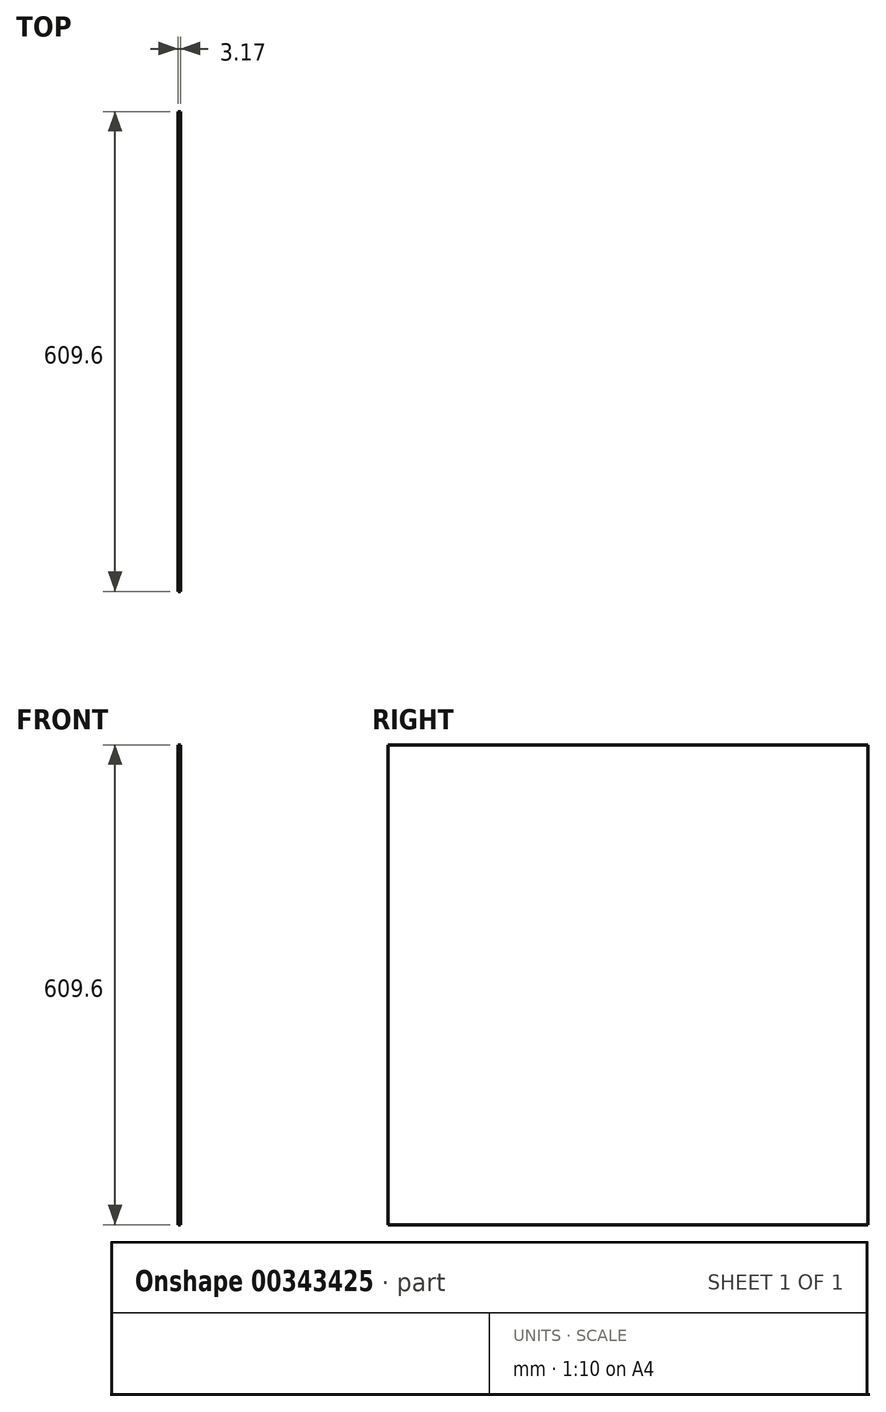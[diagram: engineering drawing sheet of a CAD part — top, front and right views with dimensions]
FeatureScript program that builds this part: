
annotation { "Feature Type Name" : "Feature", "Feature Type Description" : "" }
export const myFeature = defineFeature(function(context is Context, id is Id, definition is map)
    precondition{}
    {
        {
            var Q0;
            Q0=qCreatedBy(makeId("Right.planeOp"),FACE);
            var sketch = newSketch(context, id + "F0", { "sketchPlane" : qUnion([Q0])});
            skLineSegment(sketch, "E0.bottom", {"start": v(0, 0) * mm, "end": v(609.6, 0) * mm});
            skLineSegment(sketch, "E0.top", {"start": v(0, -609.6) * mm, "end": v(609.6, -609.6) * mm});
            skLineSegment(sketch, "E0.left", {"start": v(0, 0) * mm, "end": v(0, -609.6) * mm});
            skLineSegment(sketch, "E0.right", {"start": v(609.6, 0) * mm, "end": v(609.6, -609.6) * mm});
            skSolve(sketch);
        }
        {
            var Q0;
            Q0=makeQuery(id+"F0.imprint","IMPRINT",FACE,{"disambiguationData":[TD([[makeQuery(id+"F0.imprint","IMPRINT",EDGE,{"derivedFrom":sQuery(id+"F0.wireOp",EDGE,"E0.bottom")}),-1.0]])]});
            extrude(context, id + "F1", {"entities" : qUnion([Q0]), "depth" : 3.17 * mm});
        }
    });
